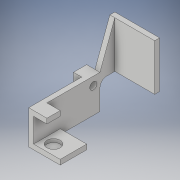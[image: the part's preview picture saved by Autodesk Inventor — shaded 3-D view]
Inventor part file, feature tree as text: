
AUTODESK INVENTOR PART (.ipt)
format: ipt  version: 2017 (Build 210142000, 142)  size: 191,488 bytes
history: native  units: in
note: dims shown in document units (in); Inventor stores cm internally (conversion verified against a paired STEP export)
features: sketch x8, projected_geometry x8, extrude x6, hole x2, fillet x1
ambient origin geometry x8: Origin, YZ Plane, XZ Plane, XY Plane, X Axis, Y Axis, Z Axis, Center Point
bodies: Solid1 (feature_tree)
feature tree (25):
  extrude  "Extrusion1"  Depth=2.5in
  extrude  "Extrusion2"  Depth=0.5in
  extrude  "Extrusion3"  Depth=0.5in TaperAngle=0.0deg
  extrude  "Extrusion4"  Depth=1.0in TaperAngle=0.0deg
  hole  "Hole1"  [1 undecoded]
  hole  "Hole2"  [1 undecoded]
  extrude  "Extrusion6"  Depth=0.25in
  extrude  "Extrusion7"  Depth=0.375in
  fillet  "Fillet1"  Radius=0.375in
  sketch  "Sketch1"  dims[d0=1.2813in d1=2.5in]
  sketch  "Sketch2"  dims[d2=0.1875in d3=0.0in d4=0.5in]
  projected_geometry  "Projected Loop1"
  sketch  "Sketch3"  dims[d5=0.1875in d6=0.5in d7=0.0in]
  projected_geometry  "Projected Loop2"
  sketch  "Sketch4"  dims[d8=0.1875in d9=1.0in d10=0.0in]
  projected_geometry  "Projected Loop3"
  sketch  "Sketch5"  dims[d11=0.5in d12=0.625in]
  projected_geometry  "Projected Loop4"
  projected_geometry  "Projected Loop5"
  sketch  "Sketch6"  dims[d13=0.3125in d14=0.0in d15=0.1875in]
  projected_geometry  "Projected Loop6"
  sketch  "Sketch8"  dims[d16=0.3125in d17=0.25in]
  projected_geometry  "Projected Loop8"
  sketch  "Sketch9"  dims[d18=0.27in d19=0.75in d20=0.375in d21=0.25in d22=0.5635in d23=1.0in d24=0.8108in d25=0.375in d26=0.375in d27=0.5in d28=0.75in d29=0.375in d30=0.25in d31=0.5635in d32=0.125in d33=0.0in d39=0.1875in d40=1.75in d41=1.5in d42=0.1875in d43=0.0in d44=1.5in d45=0.0in d46=0.25in d47=1.0in]
  projected_geometry  "Projected Loop9"
note: 2 required parameter values undecoded (feature->parameter linkage not recoverable at this tier; creation-order binding heuristic only, values carry confidence <= 0.55)
